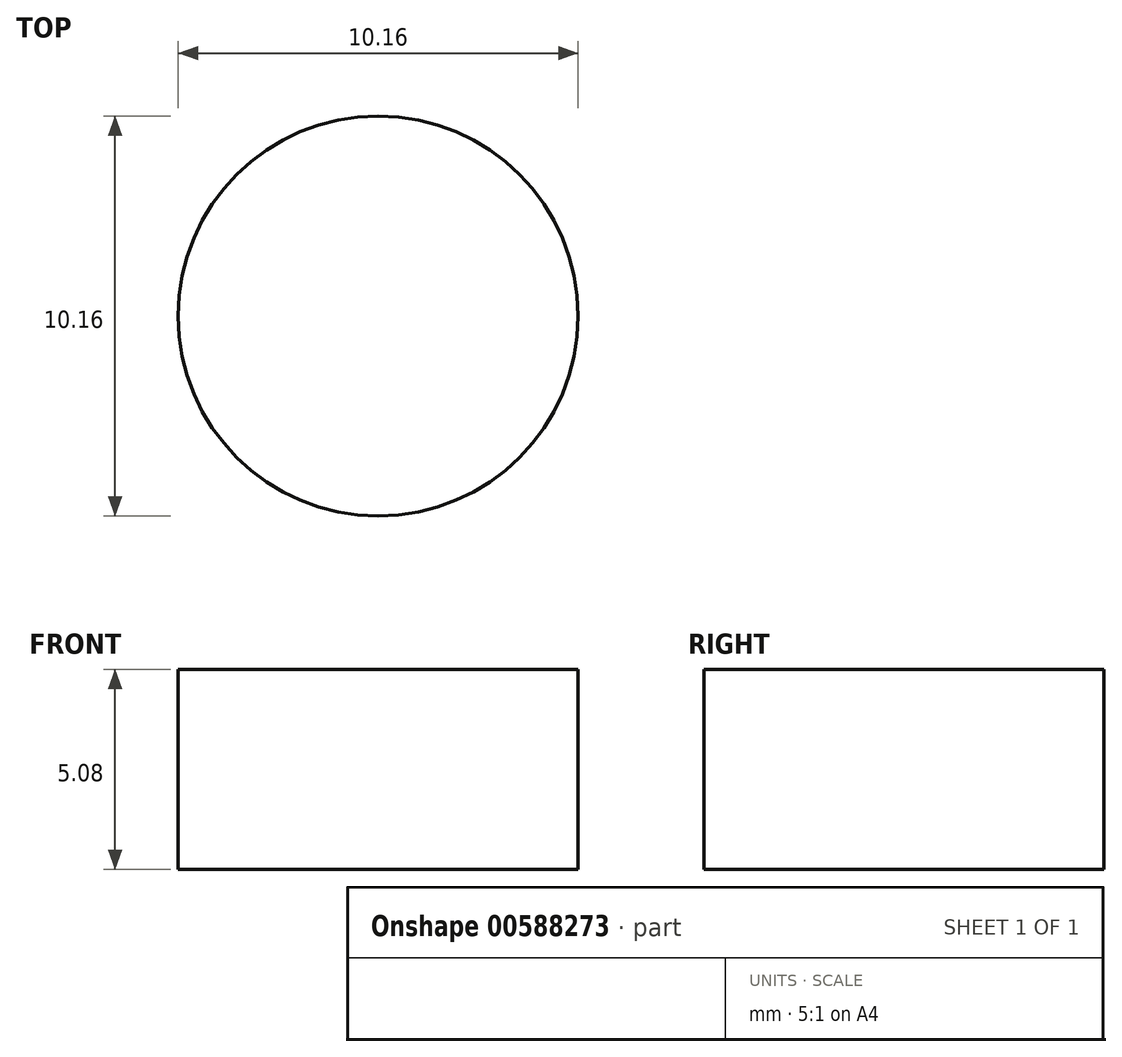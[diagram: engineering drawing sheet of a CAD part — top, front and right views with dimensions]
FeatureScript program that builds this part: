
annotation { "Feature Type Name" : "Feature", "Feature Type Description" : "" }
export const myFeature = defineFeature(function(context is Context, id is Id, definition is map)
    precondition{}
    {
        {
            var Q0;
            Q0=qCreatedBy(makeId("Top.planeOp"),FACE);
            var sketch = newSketch(context, id + "F0", { "sketchPlane" : qUnion([Q0])});
            skLineSegment(sketch, "E0", {"start": v(-0.22, 0.23) * mm, "end": v(-0.2, 0.22) * mm});
            skLineSegment(sketch, "E1", {"start": v(-0.2, 0.22) * mm, "end": v(-0.2, 0.22) * mm});
            skLineSegment(sketch, "E2", {"start": v(-0.2, 0.22) * mm, "end": v(-0.19, 0.21) * mm});
            skLineSegment(sketch, "E3", {"start": v(-0.19, 0.21) * mm, "end": v(-0.18, 0.2) * mm});
            skLineSegment(sketch, "E4", {"start": v(-0.18, 0.2) * mm, "end": v(-0.18, 0.2) * mm});
            skLineSegment(sketch, "E5", {"start": v(-0.18, 0.2) * mm, "end": v(-0.18, 0.17) * mm});
            skLineSegment(sketch, "E6", {"start": v(-0.18, 0.17) * mm, "end": v(-0.17, 0.16) * mm});
            skLineSegment(sketch, "E7", {"start": v(-0.17, 0.16) * mm, "end": v(-0.16, 0.16) * mm});
            skLineSegment(sketch, "E8", {"start": v(-0.16, 0.16) * mm, "end": v(-0.15, 0.15) * mm});
            skLineSegment(sketch, "E9", {"start": v(-0.15, 0.15) * mm, "end": v(-0.1, 0.13) * mm});
            skLineSegment(sketch, "E10", {"start": v(-0.1, 0.13) * mm, "end": v(-0.1, 0.13) * mm});
            skLineSegment(sketch, "E11", {"start": v(-0.1, 0.13) * mm, "end": v(-0.1, 0.12) * mm});
            skLineSegment(sketch, "E12", {"start": v(-0.1, 0.12) * mm, "end": v(-0.1, 0.12) * mm});
            skLineSegment(sketch, "E13", {"start": v(-0.1, 0.12) * mm, "end": v(-0.09, 0.11) * mm});
            skLineSegment(sketch, "E14", {"start": v(-0.09, 0.11) * mm, "end": v(-0.06, 0.09) * mm});
            skLineSegment(sketch, "E15", {"start": v(-0.06, 0.09) * mm, "end": v(0, 0.03) * mm});
            skLineSegment(sketch, "E16", {"start": v(0, 0.03) * mm, "end": v(0.03, -0.04) * mm});
            skLineSegment(sketch, "E17", {"start": v(0.03, -0.04) * mm, "end": v(0.07, -0.11) * mm});
            skLineSegment(sketch, "E18", {"start": v(0.07, -0.11) * mm, "end": v(0.08, -0.19) * mm});
            skLineSegment(sketch, "E19", {"start": v(0.08, -0.19) * mm, "end": v(0.09, -0.37) * mm});
            skLineSegment(sketch, "E20", {"start": v(0.09, -0.37) * mm, "end": v(0.08, -0.55) * mm});
            skLineSegment(sketch, "E21", {"start": v(0.08, -0.55) * mm, "end": v(0.07, -0.74) * mm});
            skLineSegment(sketch, "E22", {"start": v(0.07, -0.74) * mm, "end": v(0.03, -1.23) * mm});
            skLineSegment(sketch, "E23", {"start": v(0.03, -1.23) * mm, "end": v(0.02, -1.36) * mm});
            skLineSegment(sketch, "E24", {"start": v(0.02, -1.36) * mm, "end": v(0.02, -1.5) * mm});
            skLineSegment(sketch, "E25", {"start": v(0.02, -1.5) * mm, "end": v(0.02, -1.63) * mm});
            skLineSegment(sketch, "E26", {"start": v(0.02, -1.63) * mm, "end": v(0, -1.73) * mm});
            skLineSegment(sketch, "E27", {"start": v(0, -1.73) * mm, "end": v(0, -1.75) * mm});
            skLineSegment(sketch, "E28", {"start": v(0, -1.75) * mm, "end": v(-0.01, -1.77) * mm});
            skLineSegment(sketch, "E29", {"start": v(-0.01, -1.77) * mm, "end": v(-0.02, -1.77) * mm});
            skLineSegment(sketch, "E30", {"start": v(-0.02, -1.77) * mm, "end": v(-0.02, -1.77) * mm});
            skLineSegment(sketch, "E31", {"start": v(-0.02, -1.77) * mm, "end": v(-0.02, -1.78) * mm});
            skLineSegment(sketch, "E32", {"start": v(-0.02, -1.78) * mm, "end": v(-0.02, -1.77) * mm});
            skLineSegment(sketch, "E33", {"start": v(-0.02, -1.77) * mm, "end": v(-0.03, -1.77) * mm});
            skLineSegment(sketch, "E34", {"start": v(-0.03, -1.77) * mm, "end": v(-0.03, -1.77) * mm});
            skLineSegment(sketch, "E35", {"start": v(-0.03, -1.77) * mm, "end": v(-0.05, -1.74) * mm});
            skLineSegment(sketch, "E36", {"start": v(-0.05, -1.74) * mm, "end": v(-0.06, -1.67) * mm});
            skLineSegment(sketch, "E37", {"start": v(-0.06, -1.67) * mm, "end": v(-0.08, -1.6) * mm});
            skLineSegment(sketch, "E38", {"start": v(-0.08, -1.6) * mm, "end": v(-0.1, -1.43) * mm});
            skLineSegment(sketch, "E39", {"start": v(-0.1, -1.43) * mm, "end": v(-0.12, -1.26) * mm});
            skLineSegment(sketch, "E40", {"start": v(-0.12, -1.26) * mm, "end": v(-0.17, -0.91) * mm});
            skLineSegment(sketch, "E41", {"start": v(-0.17, -0.91) * mm, "end": v(-0.18, -0.83) * mm});
            skLineSegment(sketch, "E42", {"start": v(-0.18, -0.83) * mm, "end": v(-0.18, -0.78) * mm});
            skLineSegment(sketch, "E43", {"start": v(-0.18, -0.78) * mm, "end": v(-0.19, -0.76) * mm});
            skLineSegment(sketch, "E44", {"start": v(-0.19, -0.76) * mm, "end": v(-0.19, -0.76) * mm});
            skLineSegment(sketch, "E45", {"start": v(-0.19, -0.76) * mm, "end": v(-0.2, -0.75) * mm});
            skLineSegment(sketch, "E46", {"start": v(-0.2, -0.75) * mm, "end": v(-0.2, -0.75) * mm});
            skLineSegment(sketch, "E47", {"start": v(-0.2, -0.75) * mm, "end": v(-0.2, -0.74) * mm});
            skLineSegment(sketch, "E48", {"start": v(-0.2, -0.74) * mm, "end": v(-0.2, -0.74) * mm});
            skLineSegment(sketch, "E49", {"start": v(-0.2, -0.74) * mm, "end": v(-0.2, -0.73) * mm});
            skLineSegment(sketch, "E50", {"start": v(-0.2, -0.73) * mm, "end": v(-0.22, -0.68) * mm});
            skLineSegment(sketch, "E51", {"start": v(-0.22, -0.68) * mm, "end": v(-0.26, -0.48) * mm});
            skLineSegment(sketch, "E52", {"start": v(-0.26, -0.48) * mm, "end": v(-0.28, -0.34) * mm});
            skLineSegment(sketch, "E53", {"start": v(-0.28, -0.34) * mm, "end": v(-0.3, -0.2) * mm});
            skLineSegment(sketch, "E54", {"start": v(-0.3, -0.2) * mm, "end": v(-0.3, -0.07) * mm});
            skLineSegment(sketch, "E55", {"start": v(-0.3, -0.07) * mm, "end": v(-0.3, 0.07) * mm});
            skLineSegment(sketch, "E56", {"start": v(-0.3, 0.07) * mm, "end": v(-0.28, 0.12) * mm});
            skLineSegment(sketch, "E57", {"start": v(-0.28, 0.12) * mm, "end": v(-0.27, 0.16) * mm});
            skLineSegment(sketch, "E58", {"start": v(-0.27, 0.16) * mm, "end": v(-0.25, 0.2) * mm});
            skLineSegment(sketch, "E59", {"start": v(-0.25, 0.2) * mm, "end": v(-0.22, 0.23) * mm});
            skLineSegment(sketch, "E60", {"start": v(1.9, 5.51) * mm, "end": v(1.92, 5.46) * mm});
            skLineSegment(sketch, "E61", {"start": v(1.92, 5.46) * mm, "end": v(1.92, 5.43) * mm});
            skLineSegment(sketch, "E62", {"start": v(1.92, 5.43) * mm, "end": v(1.92, 5.4) * mm});
            skLineSegment(sketch, "E63", {"start": v(1.92, 5.4) * mm, "end": v(1.92, 5.4) * mm});
            skLineSegment(sketch, "E64", {"start": v(1.92, 5.4) * mm, "end": v(1.92, 5.39) * mm});
            skLineSegment(sketch, "E65", {"start": v(1.92, 5.39) * mm, "end": v(1.93, 5.34) * mm});
            skLineSegment(sketch, "E66", {"start": v(1.93, 5.34) * mm, "end": v(1.95, 5.12) * mm});
            skLineSegment(sketch, "E67", {"start": v(1.95, 5.12) * mm, "end": v(1.97, 4.94) * mm});
            skLineSegment(sketch, "E68", {"start": v(1.97, 4.94) * mm, "end": v(2, 4.77) * mm});
            skLineSegment(sketch, "E69", {"start": v(2, 4.77) * mm, "end": v(2, 4.6) * mm});
            skLineSegment(sketch, "E70", {"start": v(2, 4.6) * mm, "end": v(2, 4.42) * mm});
            skLineSegment(sketch, "E71", {"start": v(2, 4.42) * mm, "end": v(2, 4.25) * mm});
            skLineSegment(sketch, "E72", {"start": v(2, 4.25) * mm, "end": v(1.96, 4.1) * mm});
            skLineSegment(sketch, "E73", {"start": v(1.96, 4.1) * mm, "end": v(1.92, 3.97) * mm});
            skLineSegment(sketch, "E74", {"start": v(1.92, 3.97) * mm, "end": v(1.86, 3.84) * mm});
            skLineSegment(sketch, "E75", {"start": v(1.86, 3.84) * mm, "end": v(1.8, 3.7) * mm});
            skLineSegment(sketch, "E76", {"start": v(1.8, 3.7) * mm, "end": v(1.68, 3.52) * mm});
            skLineSegment(sketch, "E77", {"start": v(1.68, 3.52) * mm, "end": v(1.56, 3.33) * mm});
            skLineSegment(sketch, "E78", {"start": v(1.56, 3.33) * mm, "end": v(1.43, 3.14) * mm});
            skLineSegment(sketch, "E79", {"start": v(1.43, 3.14) * mm, "end": v(1.3, 2.95) * mm});
            skLineSegment(sketch, "E80", {"start": v(1.3, 2.95) * mm, "end": v(1.2, 2.76) * mm});
            skLineSegment(sketch, "E81", {"start": v(1.2, 2.76) * mm, "end": v(1.15, 2.65) * mm});
            skLineSegment(sketch, "E82", {"start": v(1.15, 2.65) * mm, "end": v(1.1, 2.54) * mm});
            skLineSegment(sketch, "E83", {"start": v(1.1, 2.54) * mm, "end": v(1.1, 2.49) * mm});
            skLineSegment(sketch, "E84", {"start": v(1.1, 2.49) * mm, "end": v(1.1, 2.43) * mm});
            skLineSegment(sketch, "E85", {"start": v(1.1, 2.43) * mm, "end": v(1.11, 2.37) * mm});
            skLineSegment(sketch, "E86", {"start": v(1.11, 2.37) * mm, "end": v(1.13, 2.3) * mm});
            skLineSegment(sketch, "E87", {"start": v(1.13, 2.3) * mm, "end": v(1.16, 2.22) * mm});
            skLineSegment(sketch, "E88", {"start": v(1.16, 2.22) * mm, "end": v(1.19, 2.13) * mm});
            skLineSegment(sketch, "E89", {"start": v(1.19, 2.13) * mm, "end": v(1.2, 2.04) * mm});
            skLineSegment(sketch, "E90", {"start": v(1.2, 2.04) * mm, "end": v(1.2, 1.87) * mm});
            skLineSegment(sketch, "E91", {"start": v(1.2, 1.87) * mm, "end": v(1.17, 1.7) * mm});
            skLineSegment(sketch, "E92", {"start": v(1.17, 1.7) * mm, "end": v(1.13, 1.52) * mm});
            skLineSegment(sketch, "E93", {"start": v(1.13, 1.52) * mm, "end": v(1.1, 1.34) * mm});
            skLineSegment(sketch, "E94", {"start": v(1.1, 1.34) * mm, "end": v(1.05, 1.12) * mm});
            skLineSegment(sketch, "E95", {"start": v(1.05, 1.12) * mm, "end": v(1.03, 0.9) * mm});
            skLineSegment(sketch, "E96", {"start": v(1.03, 0.9) * mm, "end": v(1.02, 0.67) * mm});
            skLineSegment(sketch, "E97", {"start": v(1.02, 0.67) * mm, "end": v(1.02, 0.5) * mm});
            skLineSegment(sketch, "E98", {"start": v(1.02, 0.5) * mm, "end": v(1, 0.33) * mm});
            skLineSegment(sketch, "E99", {"start": v(1, 0.33) * mm, "end": v(0.99, 0.16) * mm});
            skLineSegment(sketch, "E100", {"start": v(0.99, 0.16) * mm, "end": v(0.95, 0) * mm});
            skLineSegment(sketch, "E101", {"start": v(0.6, 3.64) * mm, "end": v(0.85, 3.9) * mm});
            skLineSegment(sketch, "E102", {"start": v(0.85, 3.9) * mm, "end": v(1.1, 4.16) * mm});
            skLineSegment(sketch, "E103", {"start": v(1.1, 4.16) * mm, "end": v(1.25, 4.32) * mm});
            skLineSegment(sketch, "E104", {"start": v(1.25, 4.32) * mm, "end": v(1.4, 4.5) * mm});
            skLineSegment(sketch, "E105", {"start": v(1.4, 4.5) * mm, "end": v(1.54, 4.67) * mm});
            skLineSegment(sketch, "E106", {"start": v(1.54, 4.67) * mm, "end": v(1.62, 4.8) * mm});
            skLineSegment(sketch, "E107", {"start": v(1.62, 4.8) * mm, "end": v(1.68, 4.94) * mm});
            skLineSegment(sketch, "E108", {"start": v(1.68, 4.94) * mm, "end": v(1.74, 5.08) * mm});
            skLineSegment(sketch, "E109", {"start": v(1.74, 5.08) * mm, "end": v(1.82, 5.3) * mm});
            skLineSegment(sketch, "E110", {"start": v(1.82, 5.3) * mm, "end": v(1.9, 5.51) * mm});
            skLineSegment(sketch, "E111", {"start": v(0.52, 4.34) * mm, "end": v(0.6, 3.64) * mm});
            skLineSegment(sketch, "E112", {"start": v(1.73, 6.2) * mm, "end": v(1.73, 6.04) * mm});
            skLineSegment(sketch, "E113", {"start": v(1.73, 6.04) * mm, "end": v(1.74, 5.88) * mm});
            skLineSegment(sketch, "E114", {"start": v(1.74, 5.88) * mm, "end": v(1.74, 5.72) * mm});
            skLineSegment(sketch, "E115", {"start": v(1.74, 5.72) * mm, "end": v(1.73, 5.63) * mm});
            skLineSegment(sketch, "E116", {"start": v(1.73, 5.63) * mm, "end": v(1.7, 5.53) * mm});
            skLineSegment(sketch, "E117", {"start": v(1.7, 5.53) * mm, "end": v(1.64, 5.42) * mm});
            skLineSegment(sketch, "E118", {"start": v(1.64, 5.42) * mm, "end": v(1.56, 5.32) * mm});
            skLineSegment(sketch, "E119", {"start": v(1.56, 5.32) * mm, "end": v(1.39, 5.14) * mm});
            skLineSegment(sketch, "E120", {"start": v(1.39, 5.14) * mm, "end": v(1.2, 4.96) * mm});
            skLineSegment(sketch, "E121", {"start": v(1.2, 4.96) * mm, "end": v(1, 4.78) * mm});
            skLineSegment(sketch, "E122", {"start": v(1, 4.78) * mm, "end": v(0.8, 4.6) * mm});
            skLineSegment(sketch, "E123", {"start": v(0.8, 4.6) * mm, "end": v(0.52, 4.34) * mm});
            skLineSegment(sketch, "E124", {"start": v(0.1, 6.27) * mm, "end": v(0.45, 6.31) * mm});
            skLineSegment(sketch, "E125", {"start": v(0.45, 6.31) * mm, "end": v(0.8, 6.36) * mm});
            skLineSegment(sketch, "E126", {"start": v(0.8, 6.36) * mm, "end": v(0.96, 6.38) * mm});
            skLineSegment(sketch, "E127", {"start": v(0.96, 6.38) * mm, "end": v(1.13, 6.4) * mm});
            skLineSegment(sketch, "E128", {"start": v(1.13, 6.4) * mm, "end": v(1.3, 6.4) * mm});
            skLineSegment(sketch, "E129", {"start": v(1.3, 6.4) * mm, "end": v(1.44, 6.4) * mm});
            skLineSegment(sketch, "E130", {"start": v(1.44, 6.4) * mm, "end": v(1.48, 6.4) * mm});
            skLineSegment(sketch, "E131", {"start": v(1.48, 6.4) * mm, "end": v(1.52, 6.38) * mm});
            skLineSegment(sketch, "E132", {"start": v(1.52, 6.38) * mm, "end": v(1.56, 6.36) * mm});
            skLineSegment(sketch, "E133", {"start": v(1.56, 6.36) * mm, "end": v(1.6, 6.33) * mm});
            skLineSegment(sketch, "E134", {"start": v(1.6, 6.33) * mm, "end": v(1.66, 6.26) * mm});
            skLineSegment(sketch, "E135", {"start": v(1.66, 6.26) * mm, "end": v(1.73, 6.2) * mm});
            skLineSegment(sketch, "E136", {"start": v(-0.17, 5.86) * mm, "end": v(0.1, 6.27) * mm});
            skLineSegment(sketch, "E137", {"start": v(0.03, 5.62) * mm, "end": v(-0.17, 5.86) * mm});
            skLineSegment(sketch, "E138", {"start": v(-0.04, 5.26) * mm, "end": v(0.03, 5.62) * mm});
            skLineSegment(sketch, "E139", {"start": v(-0.22, 6.24) * mm, "end": v(-0.24, 6.08) * mm});
            skLineSegment(sketch, "E140", {"start": v(-0.24, 6.08) * mm, "end": v(-0.26, 5.92) * mm});
            skLineSegment(sketch, "E141", {"start": v(-0.26, 5.92) * mm, "end": v(-0.27, 5.76) * mm});
            skLineSegment(sketch, "E142", {"start": v(-0.27, 5.76) * mm, "end": v(-0.26, 5.65) * mm});
            skLineSegment(sketch, "E143", {"start": v(-0.26, 5.65) * mm, "end": v(-0.24, 5.6) * mm});
            skLineSegment(sketch, "E144", {"start": v(-0.24, 5.6) * mm, "end": v(-0.22, 5.57) * mm});
            skLineSegment(sketch, "E145", {"start": v(-0.22, 5.57) * mm, "end": v(-0.2, 5.55) * mm});
            skLineSegment(sketch, "E146", {"start": v(-0.2, 5.55) * mm, "end": v(-0.13, 5.5) * mm});
            skLineSegment(sketch, "E147", {"start": v(-0.13, 5.5) * mm, "end": v(-0.08, 5.45) * mm});
            skLineSegment(sketch, "E148", {"start": v(-0.08, 5.45) * mm, "end": v(-0.05, 5.41) * mm});
            skLineSegment(sketch, "E149", {"start": v(-0.05, 5.41) * mm, "end": v(-0.04, 5.36) * mm});
            skLineSegment(sketch, "E150", {"start": v(-0.04, 5.36) * mm, "end": v(-0.04, 5.31) * mm});
            skLineSegment(sketch, "E151", {"start": v(-0.04, 5.31) * mm, "end": v(-0.04, 5.26) * mm});
            skLineSegment(sketch, "E152", {"start": v(-0.76, 6.18) * mm, "end": v(-0.22, 6.24) * mm});
            skLineSegment(sketch, "E153", {"start": v(-0.98, 5.57) * mm, "end": v(-0.76, 6.18) * mm});
            skLineSegment(sketch, "E154", {"start": v(0.03, 3.57) * mm, "end": v(-0.05, 3.88) * mm});
            skLineSegment(sketch, "E155", {"start": v(-0.05, 3.88) * mm, "end": v(-0.13, 4.2) * mm});
            skLineSegment(sketch, "E156", {"start": v(-0.13, 4.2) * mm, "end": v(-0.18, 4.37) * mm});
            skLineSegment(sketch, "E157", {"start": v(-0.18, 4.37) * mm, "end": v(-0.23, 4.54) * mm});
            skLineSegment(sketch, "E158", {"start": v(-0.23, 4.54) * mm, "end": v(-0.3, 4.71) * mm});
            skLineSegment(sketch, "E159", {"start": v(-0.3, 4.71) * mm, "end": v(-0.39, 4.88) * mm});
            skLineSegment(sketch, "E160", {"start": v(-0.39, 4.88) * mm, "end": v(-0.47, 5) * mm});
            skLineSegment(sketch, "E161", {"start": v(-0.47, 5) * mm, "end": v(-0.57, 5.12) * mm});
            skLineSegment(sketch, "E162", {"start": v(-0.57, 5.12) * mm, "end": v(-0.67, 5.23) * mm});
            skLineSegment(sketch, "E163", {"start": v(-0.67, 5.23) * mm, "end": v(-0.83, 5.4) * mm});
            skLineSegment(sketch, "E164", {"start": v(-0.83, 5.4) * mm, "end": v(-0.98, 5.57) * mm});
            skLineSegment(sketch, "E165", {"start": v(-0.94, 5.1) * mm, "end": v(-0.91, 5.05) * mm});
            skLineSegment(sketch, "E166", {"start": v(-0.91, 5.05) * mm, "end": v(-0.9, 5.02) * mm});
            skLineSegment(sketch, "E167", {"start": v(-0.9, 5.02) * mm, "end": v(-0.9, 5) * mm});
            skLineSegment(sketch, "E168", {"start": v(-0.9, 5) * mm, "end": v(-0.9, 5) * mm});
            skLineSegment(sketch, "E169", {"start": v(-0.9, 5) * mm, "end": v(-0.89, 5) * mm});
            skLineSegment(sketch, "E170", {"start": v(-0.89, 5) * mm, "end": v(-0.89, 5) * mm});
            skLineSegment(sketch, "E171", {"start": v(-0.89, 5) * mm, "end": v(-0.89, 4.98) * mm});
            skLineSegment(sketch, "E172", {"start": v(-0.89, 4.98) * mm, "end": v(-0.88, 4.95) * mm});
            skLineSegment(sketch, "E173", {"start": v(-0.88, 4.95) * mm, "end": v(-0.87, 4.83) * mm});
            skLineSegment(sketch, "E174", {"start": v(-0.87, 4.83) * mm, "end": v(-0.86, 4.7) * mm});
            skLineSegment(sketch, "E175", {"start": v(-0.86, 4.7) * mm, "end": v(-0.85, 4.58) * mm});
            skLineSegment(sketch, "E176", {"start": v(-0.85, 4.58) * mm, "end": v(-0.84, 4.46) * mm});
            skLineSegment(sketch, "E177", {"start": v(-0.84, 4.46) * mm, "end": v(-0.82, 4.34) * mm});
            skLineSegment(sketch, "E178", {"start": v(-0.82, 4.34) * mm, "end": v(-0.78, 4.24) * mm});
            skLineSegment(sketch, "E179", {"start": v(-0.78, 4.24) * mm, "end": v(-0.73, 4.14) * mm});
            skLineSegment(sketch, "E180", {"start": v(-0.73, 4.14) * mm, "end": v(-0.64, 4.03) * mm});
            skLineSegment(sketch, "E181", {"start": v(-0.64, 4.03) * mm, "end": v(-0.53, 3.93) * mm});
            skLineSegment(sketch, "E182", {"start": v(-0.53, 3.93) * mm, "end": v(-0.4, 3.84) * mm});
            skLineSegment(sketch, "E183", {"start": v(-0.4, 3.84) * mm, "end": v(-0.25, 3.75) * mm});
            skLineSegment(sketch, "E184", {"start": v(-0.25, 3.75) * mm, "end": v(-0.1, 3.66) * mm});
            skLineSegment(sketch, "E185", {"start": v(-0.1, 3.66) * mm, "end": v(0.03, 3.57) * mm});
            skLineSegment(sketch, "E186", {"start": v(0.17, 0.1) * mm, "end": v(0.09, 0.2) * mm});
            skLineSegment(sketch, "E187", {"start": v(0.09, 0.2) * mm, "end": v(-0.01, 0.28) * mm});
            skLineSegment(sketch, "E188", {"start": v(-0.01, 0.28) * mm, "end": v(-0.11, 0.37) * mm});
            skLineSegment(sketch, "E189", {"start": v(-0.11, 0.37) * mm, "end": v(-0.2, 0.47) * mm});
            skLineSegment(sketch, "E190", {"start": v(-0.2, 0.47) * mm, "end": v(-0.25, 0.53) * mm});
            skLineSegment(sketch, "E191", {"start": v(-0.25, 0.53) * mm, "end": v(-0.28, 0.6) * mm});
            skLineSegment(sketch, "E192", {"start": v(-0.28, 0.6) * mm, "end": v(-0.31, 0.72) * mm});
            skLineSegment(sketch, "E193", {"start": v(-0.31, 0.72) * mm, "end": v(-0.33, 0.84) * mm});
            skLineSegment(sketch, "E194", {"start": v(-0.33, 0.84) * mm, "end": v(-0.34, 0.96) * mm});
            skLineSegment(sketch, "E195", {"start": v(-0.34, 0.96) * mm, "end": v(-0.34, 1.23) * mm});
            skLineSegment(sketch, "E196", {"start": v(-0.34, 1.23) * mm, "end": v(-0.32, 1.5) * mm});
            skLineSegment(sketch, "E197", {"start": v(-0.32, 1.5) * mm, "end": v(-0.3, 1.76) * mm});
            skLineSegment(sketch, "E198", {"start": v(-0.3, 1.76) * mm, "end": v(-0.3, 1.9) * mm});
            skLineSegment(sketch, "E199", {"start": v(-0.3, 1.9) * mm, "end": v(-0.3, 2.03) * mm});
            skLineSegment(sketch, "E200", {"start": v(-0.3, 2.03) * mm, "end": v(-0.31, 2.16) * mm});
            skLineSegment(sketch, "E201", {"start": v(-0.31, 2.16) * mm, "end": v(-0.33, 2.23) * mm});
            skLineSegment(sketch, "E202", {"start": v(-0.33, 2.23) * mm, "end": v(-0.36, 2.3) * mm});
            skLineSegment(sketch, "E203", {"start": v(-0.36, 2.3) * mm, "end": v(-0.39, 2.35) * mm});
            skLineSegment(sketch, "E204", {"start": v(-0.39, 2.35) * mm, "end": v(-0.43, 2.43) * mm});
            skLineSegment(sketch, "E205", {"start": v(-0.43, 2.43) * mm, "end": v(-0.46, 2.51) * mm});
            skLineSegment(sketch, "E206", {"start": v(-0.46, 2.51) * mm, "end": v(-0.48, 2.6) * mm});
            skLineSegment(sketch, "E207", {"start": v(-0.48, 2.6) * mm, "end": v(-0.49, 2.73) * mm});
            skLineSegment(sketch, "E208", {"start": v(-0.49, 2.73) * mm, "end": v(-0.5, 2.86) * mm});
            skLineSegment(sketch, "E209", {"start": v(-0.5, 2.86) * mm, "end": v(-0.53, 2.92) * mm});
            skLineSegment(sketch, "E210", {"start": v(-0.53, 2.92) * mm, "end": v(-0.56, 2.98) * mm});
            skLineSegment(sketch, "E211", {"start": v(-0.56, 2.98) * mm, "end": v(-0.6, 3.05) * mm});
            skLineSegment(sketch, "E212", {"start": v(-0.6, 3.05) * mm, "end": v(-0.67, 3.1) * mm});
            skLineSegment(sketch, "E213", {"start": v(-0.67, 3.1) * mm, "end": v(-0.77, 3.18) * mm});
            skLineSegment(sketch, "E214", {"start": v(-0.77, 3.18) * mm, "end": v(-0.86, 3.25) * mm});
            skLineSegment(sketch, "E215", {"start": v(-0.86, 3.25) * mm, "end": v(-0.96, 3.33) * mm});
            skLineSegment(sketch, "E216", {"start": v(-0.96, 3.33) * mm, "end": v(-1.05, 3.4) * mm});
            skLineSegment(sketch, "E217", {"start": v(-1.05, 3.4) * mm, "end": v(-1.13, 3.5) * mm});
            skLineSegment(sketch, "E218", {"start": v(-1.13, 3.5) * mm, "end": v(-1.2, 3.6) * mm});
            skLineSegment(sketch, "E219", {"start": v(-1.2, 3.6) * mm, "end": v(-1.28, 3.78) * mm});
            skLineSegment(sketch, "E220", {"start": v(-1.28, 3.78) * mm, "end": v(-1.34, 3.97) * mm});
            skLineSegment(sketch, "E221", {"start": v(-1.34, 3.97) * mm, "end": v(-1.36, 4.12) * mm});
            skLineSegment(sketch, "E222", {"start": v(-1.36, 4.12) * mm, "end": v(-1.36, 4.28) * mm});
            skLineSegment(sketch, "E223", {"start": v(-1.36, 4.28) * mm, "end": v(-1.34, 4.4) * mm});
            skLineSegment(sketch, "E224", {"start": v(-1.34, 4.4) * mm, "end": v(-1.3, 4.52) * mm});
            skLineSegment(sketch, "E225", {"start": v(-1.3, 4.52) * mm, "end": v(-1.22, 4.67) * mm});
            skLineSegment(sketch, "E226", {"start": v(-1.22, 4.67) * mm, "end": v(-1.13, 4.81) * mm});
            skLineSegment(sketch, "E227", {"start": v(-1.13, 4.81) * mm, "end": v(-1.03, 4.95) * mm});
            skLineSegment(sketch, "E228", {"start": v(-1.03, 4.95) * mm, "end": v(-0.94, 5.1) * mm});
            skLineSegment(sketch, "E229", {"start": v(0.03, -2.5) * mm, "end": v(0.17, 0.1) * mm});
            skLineSegment(sketch, "E230", {"start": v(0.3, -2.96) * mm, "end": v(0.03, -2.5) * mm});
            skLineSegment(sketch, "E231", {"start": v(0.37, -2.7) * mm, "end": v(0.3, -2.96) * mm});
            skLineSegment(sketch, "E232", {"start": v(0.32, 0.63) * mm, "end": v(0.37, -2.7) * mm});
            skLineSegment(sketch, "E233", {"start": v(0.03, 2.1) * mm, "end": v(0.2, 1.37) * mm});
            skLineSegment(sketch, "E234", {"start": v(0.2, 1.37) * mm, "end": v(0.25, 1.2) * mm});
            skLineSegment(sketch, "E235", {"start": v(0.25, 1.2) * mm, "end": v(0.29, 1) * mm});
            skLineSegment(sketch, "E236", {"start": v(0.29, 1) * mm, "end": v(0.31, 0.93) * mm});
            skLineSegment(sketch, "E237", {"start": v(0.31, 0.93) * mm, "end": v(0.34, 0.85) * mm});
            skLineSegment(sketch, "E238", {"start": v(0.34, 0.85) * mm, "end": v(0.34, 0.76) * mm});
            skLineSegment(sketch, "E239", {"start": v(0.34, 0.76) * mm, "end": v(0.32, 0.63) * mm});
            skLineSegment(sketch, "E240", {"start": v(0.4, 0.99) * mm, "end": v(0.37, 1.23) * mm});
            skLineSegment(sketch, "E241", {"start": v(0.37, 1.23) * mm, "end": v(0.33, 1.48) * mm});
            skLineSegment(sketch, "E242", {"start": v(0.33, 1.48) * mm, "end": v(0.29, 1.72) * mm});
            skLineSegment(sketch, "E243", {"start": v(0.29, 1.72) * mm, "end": v(0.26, 1.82) * mm});
            skLineSegment(sketch, "E244", {"start": v(0.26, 1.82) * mm, "end": v(0.23, 1.93) * mm});
            skLineSegment(sketch, "E245", {"start": v(0.23, 1.93) * mm, "end": v(0.2, 2.02) * mm});
            skLineSegment(sketch, "E246", {"start": v(0.2, 2.02) * mm, "end": v(0.17, 2.04) * mm});
            skLineSegment(sketch, "E247", {"start": v(0.17, 2.04) * mm, "end": v(0.13, 2.07) * mm});
            skLineSegment(sketch, "E248", {"start": v(0.13, 2.07) * mm, "end": v(0.08, 2.09) * mm});
            skLineSegment(sketch, "E249", {"start": v(0.08, 2.09) * mm, "end": v(0.03, 2.1) * mm});
            skLineSegment(sketch, "E250", {"start": v(0.79, 2.23) * mm, "end": v(0.4, 0.99) * mm});
            skLineSegment(sketch, "E251", {"start": v(0.63, 1.3) * mm, "end": v(0.79, 2.23) * mm});
            skLineSegment(sketch, "E252", {"start": v(0.54, -3) * mm, "end": v(0.63, 1.3) * mm});
            skLineSegment(sketch, "E253", {"start": v(0.86, -3.05) * mm, "end": v(0.54, -3) * mm});
            skLineSegment(sketch, "E254", {"start": v(0.8, -0.42) * mm, "end": v(0.86, -3.05) * mm});
            skLineSegment(sketch, "E255", {"start": v(0.88, -0.21) * mm, "end": v(0.8, -0.42) * mm});
            skLineSegment(sketch, "E256", {"start": v(1.13, -2.42) * mm, "end": v(1.1, -2.4) * mm});
            skLineSegment(sketch, "E257", {"start": v(1.1, -2.4) * mm, "end": v(1.07, -2.38) * mm});
            skLineSegment(sketch, "E258", {"start": v(1.07, -2.38) * mm, "end": v(1.06, -2.36) * mm});
            skLineSegment(sketch, "E259", {"start": v(1.06, -2.36) * mm, "end": v(1.06, -2.35) * mm});
            skLineSegment(sketch, "E260", {"start": v(1.06, -2.35) * mm, "end": v(1.06, -2.35) * mm});
            skLineSegment(sketch, "E261", {"start": v(1.06, -2.35) * mm, "end": v(1.06, -2.34) * mm});
            skLineSegment(sketch, "E262", {"start": v(1.06, -2.34) * mm, "end": v(1.06, -2.33) * mm});
            skLineSegment(sketch, "E263", {"start": v(1.06, -2.33) * mm, "end": v(1.06, -2.28) * mm});
            skLineSegment(sketch, "E264", {"start": v(1.06, -2.28) * mm, "end": v(1.07, -2.09) * mm});
            skLineSegment(sketch, "E265", {"start": v(1.07, -2.09) * mm, "end": v(1.1, -1.83) * mm});
            skLineSegment(sketch, "E266", {"start": v(1.1, -1.83) * mm, "end": v(1.1, -1.76) * mm});
            skLineSegment(sketch, "E267", {"start": v(1.1, -1.76) * mm, "end": v(1.1, -1.7) * mm});
            skLineSegment(sketch, "E268", {"start": v(1.1, -1.7) * mm, "end": v(1.07, -1.63) * mm});
            skLineSegment(sketch, "E269", {"start": v(1.07, -1.63) * mm, "end": v(1.05, -1.57) * mm});
            skLineSegment(sketch, "E270", {"start": v(1.05, -1.57) * mm, "end": v(1.02, -1.43) * mm});
            skLineSegment(sketch, "E271", {"start": v(1.02, -1.43) * mm, "end": v(1, -1.3) * mm});
            skLineSegment(sketch, "E272", {"start": v(1, -1.3) * mm, "end": v(1, -1.16) * mm});
            skLineSegment(sketch, "E273", {"start": v(1, -1.16) * mm, "end": v(0.97, -0.76) * mm});
            skLineSegment(sketch, "E274", {"start": v(0.97, -0.76) * mm, "end": v(0.95, -0.62) * mm});
            skLineSegment(sketch, "E275", {"start": v(0.95, -0.62) * mm, "end": v(0.93, -0.48) * mm});
            skLineSegment(sketch, "E276", {"start": v(0.93, -0.48) * mm, "end": v(0.9, -0.4) * mm});
            skLineSegment(sketch, "E277", {"start": v(0.9, -0.4) * mm, "end": v(0.89, -0.3) * mm});
            skLineSegment(sketch, "E278", {"start": v(0.89, -0.3) * mm, "end": v(0.88, -0.21) * mm});
            skLineSegment(sketch, "E279", {"start": v(0.95, 0) * mm, "end": v(0.98, 0.02) * mm});
            skLineSegment(sketch, "E280", {"start": v(0.98, 0.02) * mm, "end": v(1, 0.03) * mm});
            skLineSegment(sketch, "E281", {"start": v(1, 0.03) * mm, "end": v(1, 0.03) * mm});
            skLineSegment(sketch, "E282", {"start": v(1, 0.03) * mm, "end": v(1, 0.04) * mm});
            skLineSegment(sketch, "E283", {"start": v(1, 0.04) * mm, "end": v(1.02, 0.05) * mm});
            skLineSegment(sketch, "E284", {"start": v(1.02, 0.05) * mm, "end": v(1.1, 0.08) * mm});
            skLineSegment(sketch, "E285", {"start": v(1.1, 0.08) * mm, "end": v(1.13, 0.1) * mm});
            skLineSegment(sketch, "E286", {"start": v(1.13, 0.1) * mm, "end": v(1.16, 0.1) * mm});
            skLineSegment(sketch, "E287", {"start": v(1.16, 0.1) * mm, "end": v(1.19, 0.09) * mm});
            skLineSegment(sketch, "E288", {"start": v(1.19, 0.09) * mm, "end": v(1.2, 0.07) * mm});
            skLineSegment(sketch, "E289", {"start": v(1.2, 0.07) * mm, "end": v(1.23, 0.04) * mm});
            skLineSegment(sketch, "E290", {"start": v(1.23, 0.04) * mm, "end": v(1.24, 0) * mm});
            skLineSegment(sketch, "E291", {"start": v(1.24, 0) * mm, "end": v(1.25, -0.05) * mm});
            skLineSegment(sketch, "E292", {"start": v(1.25, -0.05) * mm, "end": v(1.27, -0.18) * mm});
            skLineSegment(sketch, "E293", {"start": v(1.27, -0.18) * mm, "end": v(1.28, -0.32) * mm});
            skLineSegment(sketch, "E294", {"start": v(1.28, -0.32) * mm, "end": v(1.3, -0.45) * mm});
            skLineSegment(sketch, "E295", {"start": v(1.3, -0.45) * mm, "end": v(1.32, -0.64) * mm});
            skLineSegment(sketch, "E296", {"start": v(1.32, -0.64) * mm, "end": v(1.32, -0.82) * mm});
            skLineSegment(sketch, "E297", {"start": v(1.32, -0.82) * mm, "end": v(1.3, -1) * mm});
            skLineSegment(sketch, "E298", {"start": v(1.3, -1) * mm, "end": v(1.29, -1.15) * mm});
            skLineSegment(sketch, "E299", {"start": v(1.29, -1.15) * mm, "end": v(1.28, -1.29) * mm});
            skLineSegment(sketch, "E300", {"start": v(1.28, -1.29) * mm, "end": v(1.28, -1.47) * mm});
            skLineSegment(sketch, "E301", {"start": v(1.28, -1.47) * mm, "end": v(1.3, -1.66) * mm});
            skLineSegment(sketch, "E302", {"start": v(1.3, -1.66) * mm, "end": v(1.3, -1.84) * mm});
            skLineSegment(sketch, "E303", {"start": v(1.3, -1.84) * mm, "end": v(1.3, -1.97) * mm});
            skLineSegment(sketch, "E304", {"start": v(1.3, -1.97) * mm, "end": v(1.28, -2.1) * mm});
            skLineSegment(sketch, "E305", {"start": v(1.28, -2.1) * mm, "end": v(1.26, -2.2) * mm});
            skLineSegment(sketch, "E306", {"start": v(1.26, -2.2) * mm, "end": v(1.22, -2.3) * mm});
            skLineSegment(sketch, "E307", {"start": v(1.22, -2.3) * mm, "end": v(1.18, -2.37) * mm});
            skLineSegment(sketch, "E308", {"start": v(1.18, -2.37) * mm, "end": v(1.13, -2.42) * mm});
            skLineSegment(sketch, "E309", {"start": v(-1.41, 3.4) * mm, "end": v(-0.65, 2.63) * mm});
            skLineSegment(sketch, "E310", {"start": v(-2.38, -0.16) * mm, "end": v(-2.5, -0.03) * mm});
            skLineSegment(sketch, "E311", {"start": v(-2.5, -0.03) * mm, "end": v(-2.6, 0.12) * mm});
            skLineSegment(sketch, "E312", {"start": v(-2.6, 0.12) * mm, "end": v(-2.66, 0.23) * mm});
            skLineSegment(sketch, "E313", {"start": v(-2.66, 0.23) * mm, "end": v(-2.72, 0.34) * mm});
            skLineSegment(sketch, "E314", {"start": v(-2.72, 0.34) * mm, "end": v(-2.76, 0.46) * mm});
            skLineSegment(sketch, "E315", {"start": v(-2.76, 0.46) * mm, "end": v(-2.79, 0.6) * mm});
            skLineSegment(sketch, "E316", {"start": v(-2.79, 0.6) * mm, "end": v(-2.8, 0.73) * mm});
            skLineSegment(sketch, "E317", {"start": v(-2.8, 0.73) * mm, "end": v(-2.8, 0.86) * mm});
            skLineSegment(sketch, "E318", {"start": v(-2.8, 0.86) * mm, "end": v(-2.79, 1.06) * mm});
            skLineSegment(sketch, "E319", {"start": v(-2.79, 1.06) * mm, "end": v(-2.75, 1.26) * mm});
            skLineSegment(sketch, "E320", {"start": v(-2.75, 1.26) * mm, "end": v(-2.7, 1.46) * mm});
            skLineSegment(sketch, "E321", {"start": v(-2.7, 1.46) * mm, "end": v(-2.6, 1.78) * mm});
            skLineSegment(sketch, "E322", {"start": v(-2.6, 1.78) * mm, "end": v(-2.48, 2.1) * mm});
            skLineSegment(sketch, "E323", {"start": v(-2.48, 2.1) * mm, "end": v(-2.3, 2.45) * mm});
            skLineSegment(sketch, "E324", {"start": v(-2.3, 2.45) * mm, "end": v(-2.1, 2.8) * mm});
            skLineSegment(sketch, "E325", {"start": v(-2.1, 2.8) * mm, "end": v(-2.05, 2.89) * mm});
            skLineSegment(sketch, "E326", {"start": v(-2.05, 2.89) * mm, "end": v(-2, 2.98) * mm});
            skLineSegment(sketch, "E327", {"start": v(-2, 2.98) * mm, "end": v(-1.93, 3.07) * mm});
            skLineSegment(sketch, "E328", {"start": v(-1.93, 3.07) * mm, "end": v(-1.86, 3.15) * mm});
            skLineSegment(sketch, "E329", {"start": v(-1.86, 3.15) * mm, "end": v(-1.8, 3.2) * mm});
            skLineSegment(sketch, "E330", {"start": v(-1.8, 3.2) * mm, "end": v(-1.72, 3.25) * mm});
            skLineSegment(sketch, "E331", {"start": v(-1.72, 3.25) * mm, "end": v(-1.64, 3.28) * mm});
            skLineSegment(sketch, "E332", {"start": v(-1.64, 3.28) * mm, "end": v(-1.53, 3.34) * mm});
            skLineSegment(sketch, "E333", {"start": v(-1.53, 3.34) * mm, "end": v(-1.41, 3.4) * mm});
            skArc(sketch, "E334", {"start": v(-1.7, -0.54) * mm, "mid": v(-2.07, -0.42) * mm, "end": v(-2.38, -0.16) * mm});
            skLineSegment(sketch, "E335", {"start": v(-1.6, -0.55) * mm, "end": v(-1.7, -0.54) * mm});
            skArc(sketch, "E336", {"start": v(-0.94, -0.32) * mm, "mid": v(-1.24, -0.51) * mm, "end": v(-1.6, -0.55) * mm});
            skLineSegment(sketch, "E337", {"start": v(-0.89, -0.27) * mm, "end": v(-0.94, -0.32) * mm});
            skLineSegment(sketch, "E338", {"start": v(-1.82, 0.04) * mm, "end": v(-1.7, -0.04) * mm});
            skLineSegment(sketch, "E339", {"start": v(-1.7, -0.04) * mm, "end": v(-1.58, -0.12) * mm});
            skLineSegment(sketch, "E340", {"start": v(-1.58, -0.12) * mm, "end": v(-1.5, -0.16) * mm});
            skLineSegment(sketch, "E341", {"start": v(-1.5, -0.16) * mm, "end": v(-1.4, -0.2) * mm});
            skLineSegment(sketch, "E342", {"start": v(-1.4, -0.2) * mm, "end": v(-1.3, -0.23) * mm});
            skLineSegment(sketch, "E343", {"start": v(-1.3, -0.23) * mm, "end": v(-1.2, -0.24) * mm});
            skLineSegment(sketch, "E344", {"start": v(-1.2, -0.24) * mm, "end": v(-1.04, -0.26) * mm});
            skLineSegment(sketch, "E345", {"start": v(-1.04, -0.26) * mm, "end": v(-0.89, -0.27) * mm});
            skArc(sketch, "E346", {"start": v(-2, 0.35) * mm, "mid": v(-1.94, 0.18) * mm, "end": v(-1.82, 0.04) * mm});
            skLineSegment(sketch, "E347", {"start": v(-0.65, 2.63) * mm, "end": v(-0.9, 2.37) * mm});
            skLineSegment(sketch, "E348", {"start": v(-0.9, 2.37) * mm, "end": v(-1.16, 2.12) * mm});
            skLineSegment(sketch, "E349", {"start": v(-1.16, 2.12) * mm, "end": v(-1.42, 1.87) * mm});
            skLineSegment(sketch, "E350", {"start": v(-1.42, 1.87) * mm, "end": v(-1.58, 1.7) * mm});
            skLineSegment(sketch, "E351", {"start": v(-1.58, 1.7) * mm, "end": v(-1.73, 1.53) * mm});
            skLineSegment(sketch, "E352", {"start": v(-1.73, 1.53) * mm, "end": v(-1.87, 1.34) * mm});
            skLineSegment(sketch, "E353", {"start": v(-1.87, 1.34) * mm, "end": v(-1.93, 1.25) * mm});
            skLineSegment(sketch, "E354", {"start": v(-1.93, 1.25) * mm, "end": v(-1.98, 1.16) * mm});
            skLineSegment(sketch, "E355", {"start": v(-1.98, 1.16) * mm, "end": v(-2.03, 1.07) * mm});
            skLineSegment(sketch, "E356", {"start": v(-2.03, 1.07) * mm, "end": v(-2.06, 0.96) * mm});
            skLineSegment(sketch, "E357", {"start": v(-2.06, 0.96) * mm, "end": v(-2.07, 0.85) * mm});
            skLineSegment(sketch, "E358", {"start": v(-2.07, 0.85) * mm, "end": v(-2.06, 0.7) * mm});
            skLineSegment(sketch, "E359", {"start": v(-2.06, 0.7) * mm, "end": v(-2.04, 0.57) * mm});
            skLineSegment(sketch, "E360", {"start": v(-2.04, 0.57) * mm, "end": v(-2, 0.35) * mm});
            skLineSegment(sketch, "E361", {"start": v(2.09, 0.1) * mm, "end": v(2.07, 0.1) * mm});
            skArc(sketch, "E362", {"start": v(2.78, -0.08) * mm, "mid": v(2.41, -0.07) * mm, "end": v(2.09, 0.1) * mm});
            skLineSegment(sketch, "E363", {"start": v(2.94, -0.04) * mm, "end": v(2.78, -0.08) * mm});
            skArc(sketch, "E364", {"start": v(3.66, 0.54) * mm, "mid": v(3.37, 0.17) * mm, "end": v(2.94, -0.04) * mm});
            skLineSegment(sketch, "E365", {"start": v(2.2, 4) * mm, "end": v(2.41, 3.75) * mm});
            skLineSegment(sketch, "E366", {"start": v(2.41, 3.75) * mm, "end": v(2.64, 3.51) * mm});
            skLineSegment(sketch, "E367", {"start": v(2.64, 3.51) * mm, "end": v(2.86, 3.28) * mm});
            skLineSegment(sketch, "E368", {"start": v(2.86, 3.28) * mm, "end": v(3.02, 3.1) * mm});
            skLineSegment(sketch, "E369", {"start": v(3.02, 3.1) * mm, "end": v(3.16, 2.9) * mm});
            skLineSegment(sketch, "E370", {"start": v(3.16, 2.9) * mm, "end": v(3.3, 2.69) * mm});
            skLineSegment(sketch, "E371", {"start": v(3.3, 2.69) * mm, "end": v(3.4, 2.47) * mm});
            skLineSegment(sketch, "E372", {"start": v(3.4, 2.47) * mm, "end": v(3.5, 2.22) * mm});
            skLineSegment(sketch, "E373", {"start": v(3.5, 2.22) * mm, "end": v(3.59, 1.97) * mm});
            skLineSegment(sketch, "E374", {"start": v(3.59, 1.97) * mm, "end": v(3.65, 1.7) * mm});
            skLineSegment(sketch, "E375", {"start": v(3.65, 1.7) * mm, "end": v(3.7, 1.44) * mm});
            skLineSegment(sketch, "E376", {"start": v(3.7, 1.44) * mm, "end": v(3.73, 1.18) * mm});
            skLineSegment(sketch, "E377", {"start": v(3.73, 1.18) * mm, "end": v(3.75, 0.91) * mm});
            skLineSegment(sketch, "E378", {"start": v(3.75, 0.91) * mm, "end": v(3.74, 0.8) * mm});
            skLineSegment(sketch, "E379", {"start": v(3.74, 0.8) * mm, "end": v(3.72, 0.69) * mm});
            skLineSegment(sketch, "E380", {"start": v(3.72, 0.69) * mm, "end": v(3.69, 0.61) * mm});
            skLineSegment(sketch, "E381", {"start": v(3.69, 0.61) * mm, "end": v(3.66, 0.54) * mm});
            skLineSegment(sketch, "E382", {"start": v(2.91, 0.6) * mm, "end": v(2.92, 0.62) * mm});
            skLineSegment(sketch, "E383", {"start": v(2.92, 0.62) * mm, "end": v(2.95, 0.74) * mm});
            skLineSegment(sketch, "E384", {"start": v(2.95, 0.74) * mm, "end": v(2.99, 0.85) * mm});
            skLineSegment(sketch, "E385", {"start": v(2.99, 0.85) * mm, "end": v(3.01, 0.97) * mm});
            skLineSegment(sketch, "E386", {"start": v(3.01, 0.97) * mm, "end": v(3.02, 1.08) * mm});
            skLineSegment(sketch, "E387", {"start": v(3.02, 1.08) * mm, "end": v(3.02, 1.16) * mm});
            skLineSegment(sketch, "E388", {"start": v(3.02, 1.16) * mm, "end": v(3, 1.23) * mm});
            skLineSegment(sketch, "E389", {"start": v(3, 1.23) * mm, "end": v(2.94, 1.37) * mm});
            skLineSegment(sketch, "E390", {"start": v(2.94, 1.37) * mm, "end": v(2.86, 1.5) * mm});
            skLineSegment(sketch, "E391", {"start": v(2.86, 1.5) * mm, "end": v(2.77, 1.64) * mm});
            skLineSegment(sketch, "E392", {"start": v(2.77, 1.64) * mm, "end": v(2.63, 1.83) * mm});
            skLineSegment(sketch, "E393", {"start": v(2.63, 1.83) * mm, "end": v(2.48, 2.01) * mm});
            skLineSegment(sketch, "E394", {"start": v(2.48, 2.01) * mm, "end": v(2.32, 2.19) * mm});
            skLineSegment(sketch, "E395", {"start": v(2.32, 2.19) * mm, "end": v(2.08, 2.46) * mm});
            skLineSegment(sketch, "E396", {"start": v(2.08, 2.46) * mm, "end": v(1.89, 2.7) * mm});
            skLineSegment(sketch, "E397", {"start": v(1.89, 2.7) * mm, "end": v(1.8, 2.83) * mm});
            skLineSegment(sketch, "E398", {"start": v(1.8, 2.83) * mm, "end": v(1.75, 2.9) * mm});
            skLineSegment(sketch, "E399", {"start": v(1.75, 2.9) * mm, "end": v(1.72, 2.97) * mm});
            skLineSegment(sketch, "E400", {"start": v(1.72, 2.97) * mm, "end": v(1.7, 3.01) * mm});
            skLineSegment(sketch, "E401", {"start": v(1.7, 3.01) * mm, "end": v(1.7, 3.05) * mm});
            skLineSegment(sketch, "E402", {"start": v(1.7, 3.05) * mm, "end": v(1.7, 3.1) * mm});
            skLineSegment(sketch, "E403", {"start": v(1.7, 3.1) * mm, "end": v(1.71, 3.14) * mm});
            skLineSegment(sketch, "E404", {"start": v(1.71, 3.14) * mm, "end": v(1.77, 3.28) * mm});
            skLineSegment(sketch, "E405", {"start": v(1.77, 3.28) * mm, "end": v(1.84, 3.43) * mm});
            skLineSegment(sketch, "E406", {"start": v(1.84, 3.43) * mm, "end": v(1.96, 3.62) * mm});
            skLineSegment(sketch, "E407", {"start": v(1.96, 3.62) * mm, "end": v(2.08, 3.8) * mm});
            skLineSegment(sketch, "E408", {"start": v(2.08, 3.8) * mm, "end": v(2.2, 4) * mm});
            skArc(sketch, "E409", {"start": v(2.63, 0.3) * mm, "mid": v(2.8, 0.43) * mm, "end": v(2.91, 0.6) * mm});
            skLineSegment(sketch, "E410", {"start": v(2.07, 0.1) * mm, "end": v(2.63, 0.3) * mm});
            skArc(sketch, "E411", {"start": v(-3.15, -3.07) * mm, "mid": v(-3.15, -3.08) * mm, "end": v(-3.14, -3.08) * mm});
            skLineSegment(sketch, "E412", {"start": v(-3.15, -3.07) * mm, "end": v(-3.15, -3.06) * mm});
            skCircle(sketch, "E413", {"center": v(0.54, 1.8) * mm, "radius": 5.08 * mm});
            skLineSegment(sketch, "E414", {"start": v(0.54, -3) * mm, "end": v(0.54, -3.29) * mm});
            skSolve(sketch);
        }
        {
            var Q0;
            Q0=makeQuery(id+"F0.imprint","IMPRINT",FACE,{"disambiguationData":[TD([[makeQuery(id+"F0.imprint","IMPRINT",EDGE,{"derivedFrom":sQuery(id+"F0.wireOp",EDGE,"E60")}),1.0]])]});
            var sketch = newSketch(context, id + "F1", { "sketchPlane" : qUnion([Q0])});
            skCircle(sketch, "E415.0", {"center": v(0.54, 1.8) * mm, "radius": 5.08 * mm});
            skSolve(sketch);
        }
        {
            var Q0;
            Q0 = qSketchRegion(id + "F1", true);
            extrude(context, id + "F2", {"entities" : qUnion([Q0]), "oppositeDirection" : true, "depth" : 5.08 * mm, "offsetDistance" : 25.4 * mm});
        }
    });
